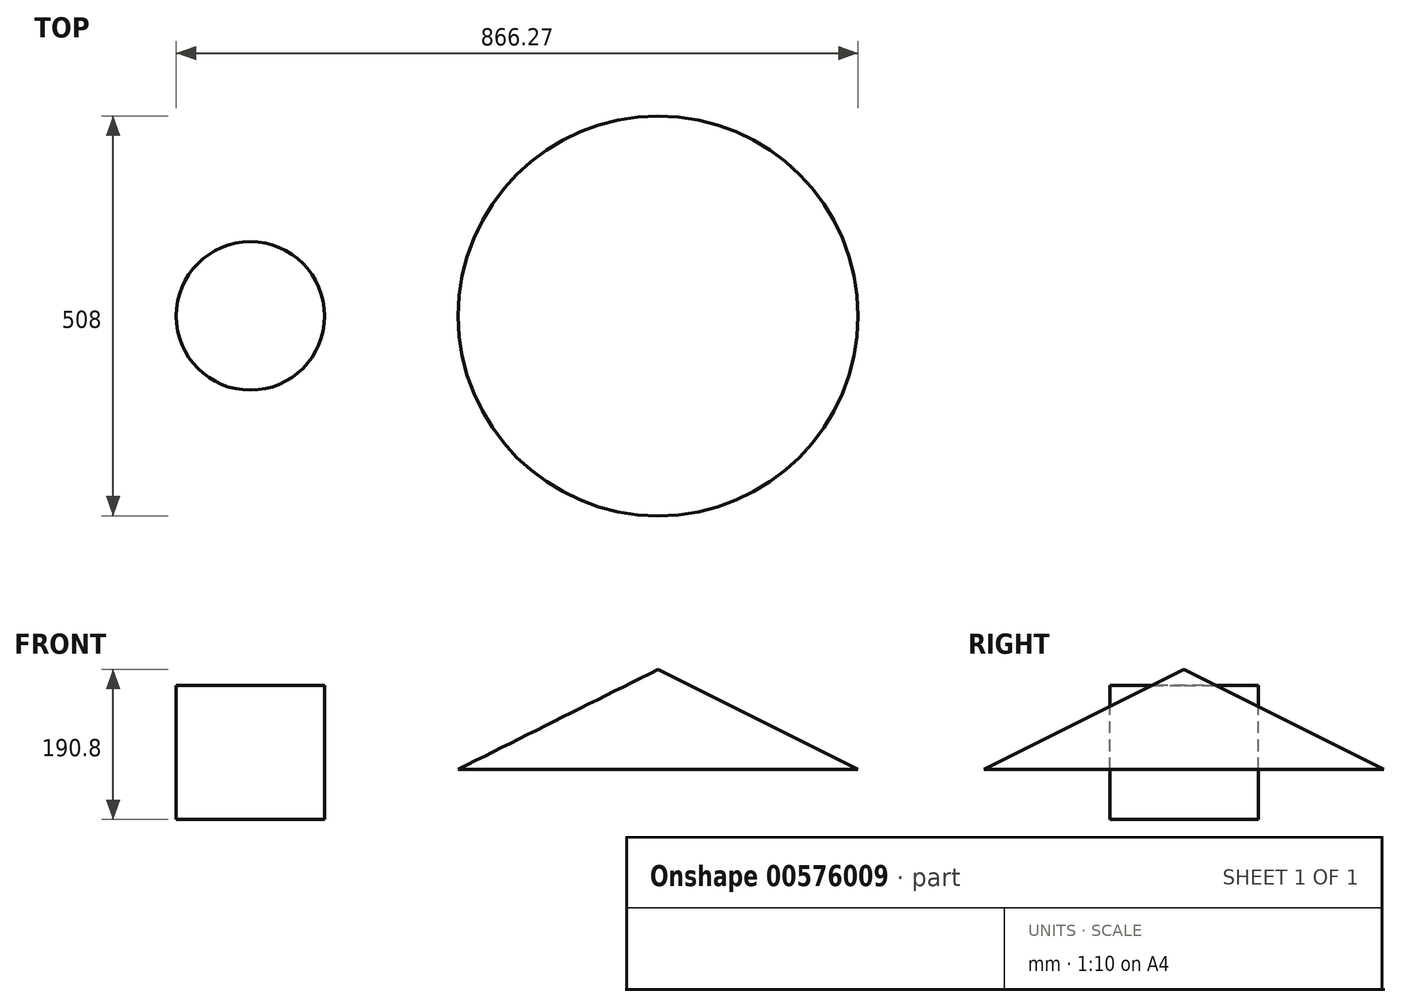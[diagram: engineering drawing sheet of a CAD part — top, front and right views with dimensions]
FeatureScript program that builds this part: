
annotation { "Feature Type Name" : "Feature", "Feature Type Description" : "" }
export const myFeature = defineFeature(function(context is Context, id is Id, definition is map)
    precondition{}
    {
        {
            var Q0;
            Q0=qCreatedBy(makeId("Front.planeOp"),FACE);
            var sketch = newSketch(context, id + "F0", { "sketchPlane" : qUnion([Q0])});
            skLineSegment(sketch, "E0", {"start": v(193.23, 138.37) * mm, "end": v(193.23, 11.37) * mm});
            skLineSegment(sketch, "E1", {"start": v(193.23, 11.37) * mm, "end": v(-60.77, 11.37) * mm});
            skLineSegment(sketch, "E2", {"start": v(-60.77, 11.37) * mm, "end": v(193.23, 138.37) * mm});
            skSolve(sketch);
        }
        {
            var Q0;
            Q0=makeQuery(id+"F0.imprint","IMPRINT",FACE,{"disambiguationData":[TD([[makeQuery(id+"F0.imprint","IMPRINT",EDGE,{"derivedFrom":sQuery(id+"F0.wireOp",EDGE,"E0")}),-1.0]])]});
            var Q1;
            Q1=sQuery(id+"F0.wireOp",EDGE,"E0");
            revolve(context, id + "F1", {"entities" : qUnion([Q0]), "axis" : qUnion([Q1]), "revolveType" : RevolveType.FULL});
        }
        {
            var Q0;
            Q0=qCreatedBy(makeId("Front.planeOp"),FACE);
            var sketch = newSketch(context, id + "F2", { "sketchPlane" : qUnion([Q0])});
            skLineSegment(sketch, "E3.bottom", {"start": v(-324.75, 117.83) * mm, "end": v(-230.46, 117.83) * mm});
            skLineSegment(sketch, "E3.top", {"start": v(-324.75, -52.43) * mm, "end": v(-230.46, -52.43) * mm});
            skLineSegment(sketch, "E3.left", {"start": v(-324.75, 117.83) * mm, "end": v(-324.75, -52.43) * mm});
            skLineSegment(sketch, "E3.right", {"start": v(-230.46, 117.83) * mm, "end": v(-230.46, -52.43) * mm});
            skSolve(sketch);
        }
        {
            var Q0;
            Q0=makeQuery(id+"F2.imprint","IMPRINT",FACE,{"disambiguationData":[TD([[makeQuery(id+"F2.imprint","IMPRINT",EDGE,{"derivedFrom":sQuery(id+"F2.wireOp",EDGE,"E3.bottom")}),-1.0]])]});
            var Q1;
            Q1=sQuery(id+"F2.wireOp",EDGE,"E3.left");
            revolve(context, id + "F3", {"entities" : qUnion([Q0]), "axis" : qUnion([Q1]), "revolveType" : RevolveType.ONE_DIRECTION, "angle" : 360 * degree});
        }
    });
